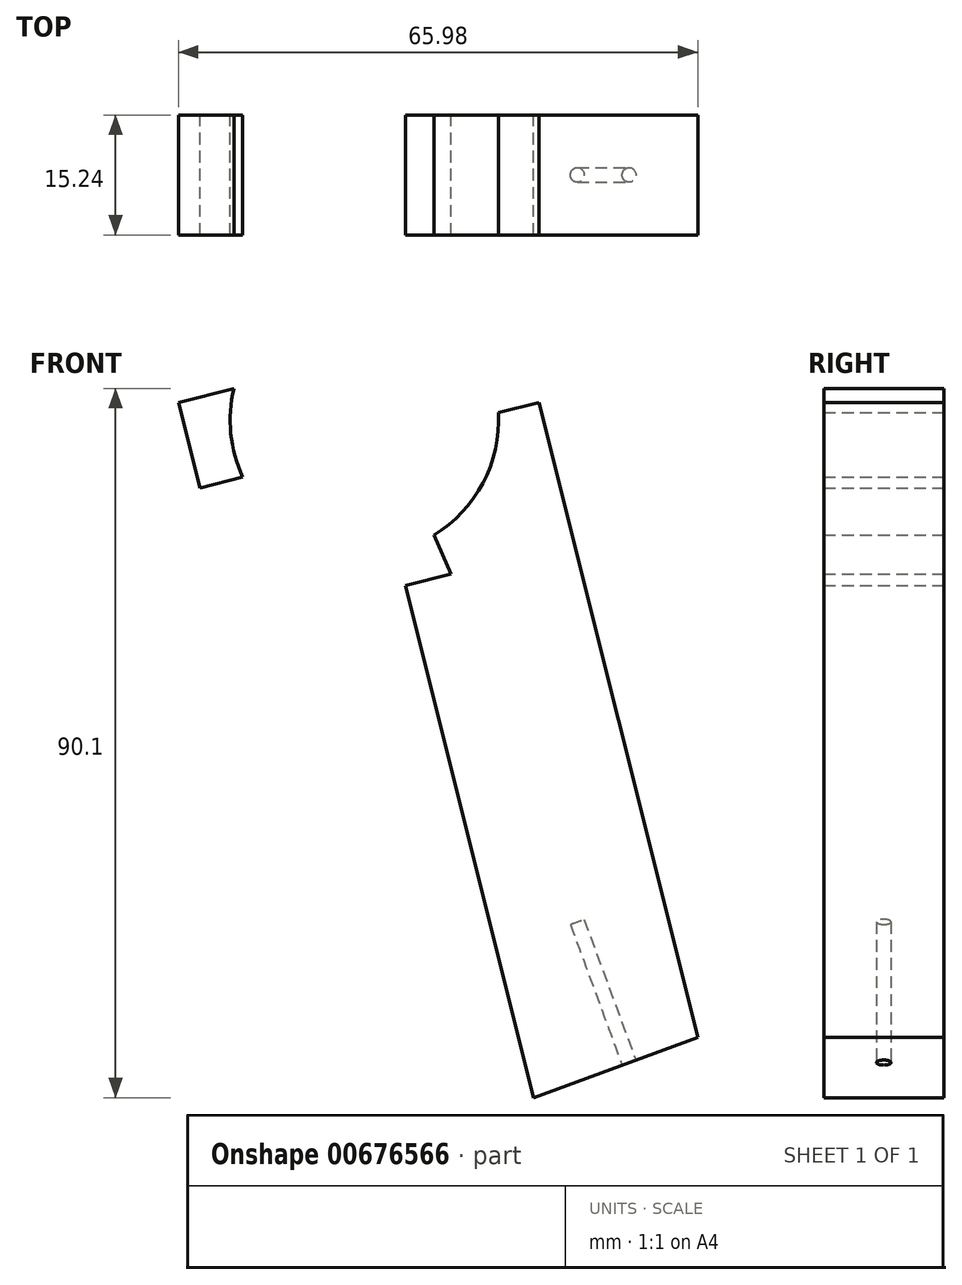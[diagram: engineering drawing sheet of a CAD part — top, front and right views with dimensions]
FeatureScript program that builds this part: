
annotation { "Feature Type Name" : "Feature", "Feature Type Description" : "" }
export const myFeature = defineFeature(function(context is Context, id is Id, definition is map)
    precondition{}
    {
        {
            var Q0;
            Q0=qCreatedBy(makeId("Front.planeOp"),FACE);
            var sketch = newSketch(context, id + "F0", { "sketchPlane" : qUnion([Q0])});
            skLineSegment(sketch, "E0", {"start": v(0, 0) * mm, "end": v(41.71, 15.36) * mm});
            skLineSegment(sketch, "E1", {"start": v(41.71, 15.36) * mm, "end": v(18.85, 106.8) * mm});
            skLineSegment(sketch, "E2", {"start": v(18.85, 106.8) * mm, "end": v(-24.27, 96.01) * mm});
            skLineSegment(sketch, "E3", {"start": v(-24.27, 96.01) * mm, "end": v(0, 0) * mm});
            skLineSegment(sketch, "E4", {"start": v(0, 0) * mm, "end": v(20.86, 7.68) * mm});
            skLineSegment(sketch, "E5", {"start": v(20.86, 7.68) * mm, "end": v(-0.66, 93.7) * mm});
            skCircle(sketch, "E6", {"center": v(-0.66, 93.7) * mm, "radius": 17.04 * mm});
            skLineSegment(sketch, "E7", {"start": v(3.48, 77.18) * mm, "end": v(-1.52, 75.93) * mm});
            skLineSegment(sketch, "E8", {"start": v(-1.52, 75.93) * mm, "end": v(3.48, 77.18) * mm});
            skLineSegment(sketch, "E9", {"start": v(3.48, 77.18) * mm, "end": v(8.16, 79.13) * mm});
            skLineSegment(sketch, "E10", {"start": v(-1.52, 75.93) * mm, "end": v(-0.4, 71.52) * mm});
            skLineSegment(sketch, "E11", {"start": v(-0.4, 71.52) * mm, "end": v(10.36, 74.22) * mm});
            skLineSegment(sketch, "E12", {"start": v(10.36, 74.22) * mm, "end": v(8.16, 79.13) * mm});
            skLineSegment(sketch, "E13", {"start": v(8.16, 79.13) * mm, "end": v(-1.52, 79.13) * mm});
            skLineSegment(sketch, "E14", {"start": v(-1.52, 79.13) * mm, "end": v(-1.52, 75.93) * mm});
            skLineSegment(sketch, "E15", {"start": v(-24.27, 96.01) * mm, "end": v(18.85, 106.8) * mm});
            skLineSegment(sketch, "E16", {"start": v(21.54, 96.01) * mm, "end": v(-21.52, 85.12) * mm});
            skLineSegment(sketch, "E17", {"start": v(-21.52, 85.12) * mm, "end": v(-24.27, 96.01) * mm});
            skSolve(sketch);
        }
        {
            var Q0;
            {var subQ4=sQuery(id+"F0.wireOp",EDGE,"E3");Q0=makeQuery(id+"F0.imprint","IMPRINT",FACE,{"disambiguationData":[TD([[makeQuery(id+"F0.imprint","IMPRINT",EDGE,{"derivedFrom":subQ4}),1.0]])]});}
            var Q1;
            {var subQ1=sQuery(id+"F0.wireOp",EDGE,"E0");Q1=makeQuery(id+"F0.imprint","IMPRINT",FACE,{"disambiguationData":[TD([[makeQuery(id+"F0.imprint","IMPRINT",EDGE,{"derivedFrom":subQ1}),1.0]])]});}
            extrude(context, id + "F1", {"entities" : qUnion([Q0, Q1]), "depth" : 15.24 * mm, "offsetDistance" : 25.4 * mm});
        }
        {
            var Q0;
            Q0=makeQuery(id+"F1.opExtrude","SWEPT_FACE",FACE,{"disambiguationData":[OSD([sQuery(id+"F0.wireOp",EDGE,"E0"),sQuery(id+"F0.wireOp",EDGE,"E4")])]});
            var sketch = newSketch(context, id + "F2", { "sketchPlane" : qUnion([Q0])});
            skLineSegment(sketch, "E18", {"start": v(0, 15.24) * mm, "end": v(0, 0) * mm});
            skLineSegment(sketch, "E19", {"start": v(0, 0) * mm, "end": v(0, 7.62) * mm});
            skLineSegment(sketch, "E20", {"start": v(0, 7.62) * mm, "end": v(44.45, 7.62) * mm});
            skCircle(sketch, "E21", {"center": v(9.49, 7.62) * mm, "radius": 0.86 * mm});
            skCircle(sketch, "E22", {"center": v(35.13, 7.62) * mm, "radius": 0.93 * mm});
            skSolve(sketch);
        }
        {
            var Q0;
            {var subQ0=sQuery(id+"F2.wireOp",EDGE,"E21");var subQ1=sQuery(id+"F2.wireOp",EDGE,"E20");var subQ2=makeQuery(id+"F2.imprint","INTERSECT",VERTEX,{"disambiguationData":[OD(0.0)],"derivedFrom":[subQ1,subQ0]});Q0=makeQuery(id+"F2.imprint","IMPRINT",FACE,{"disambiguationData":[TD([[makeQuery(id+"F2.imprint","IMPRINT",EDGE,{"disambiguationData":[TD([[subQ2,-1.0]])],"derivedFrom":subQ1}),-1.0]])]});}
            var Q1;
            {var subQ0=sQuery(id+"F2.wireOp",EDGE,"E21");var subQ1=sQuery(id+"F2.wireOp",EDGE,"E20");var subQ2=makeQuery(id+"F2.imprint","INTERSECT",VERTEX,{"disambiguationData":[OD(0.0)],"derivedFrom":[subQ1,subQ0]});Q1=makeQuery(id+"F2.imprint","IMPRINT",FACE,{"disambiguationData":[TD([[makeQuery(id+"F2.imprint","IMPRINT",EDGE,{"disambiguationData":[TD([[subQ2,-1.0]])],"derivedFrom":subQ1}),1.0]])]});}
            var Q2;
            {var subQ0=sQuery(id+"F2.wireOp",EDGE,"E22");var subQ1=sQuery(id+"F2.wireOp",EDGE,"E20");var subQ2=makeQuery(id+"F2.imprint","INTERSECT",VERTEX,{"disambiguationData":[OD(0.0)],"derivedFrom":[subQ1,subQ0]});Q2=makeQuery(id+"F2.imprint","IMPRINT",FACE,{"disambiguationData":[TD([[makeQuery(id+"F2.imprint","IMPRINT",EDGE,{"disambiguationData":[TD([[subQ2,-1.0]])],"derivedFrom":subQ1}),1.0]])]});}
            var Q3;
            {var subQ0=sQuery(id+"F2.wireOp",EDGE,"E22");var subQ1=sQuery(id+"F2.wireOp",EDGE,"E20");var subQ2=makeQuery(id+"F2.imprint","INTERSECT",VERTEX,{"disambiguationData":[OD(0.0)],"derivedFrom":[subQ1,subQ0]});Q3=makeQuery(id+"F2.imprint","IMPRINT",FACE,{"disambiguationData":[TD([[makeQuery(id+"F2.imprint","IMPRINT",EDGE,{"disambiguationData":[TD([[subQ2,-1.0]])],"derivedFrom":subQ1}),-1.0]])]});}
            extrude(context, id + "F3", {"entities" : qUnion([Q0, Q1, Q2, Q3]), "operationType" : NewBodyOperationType.REMOVE, "oppositeDirection" : true, "depth" : 19.05 * mm, "offsetDistance" : 25.4 * mm});
        }
    });
